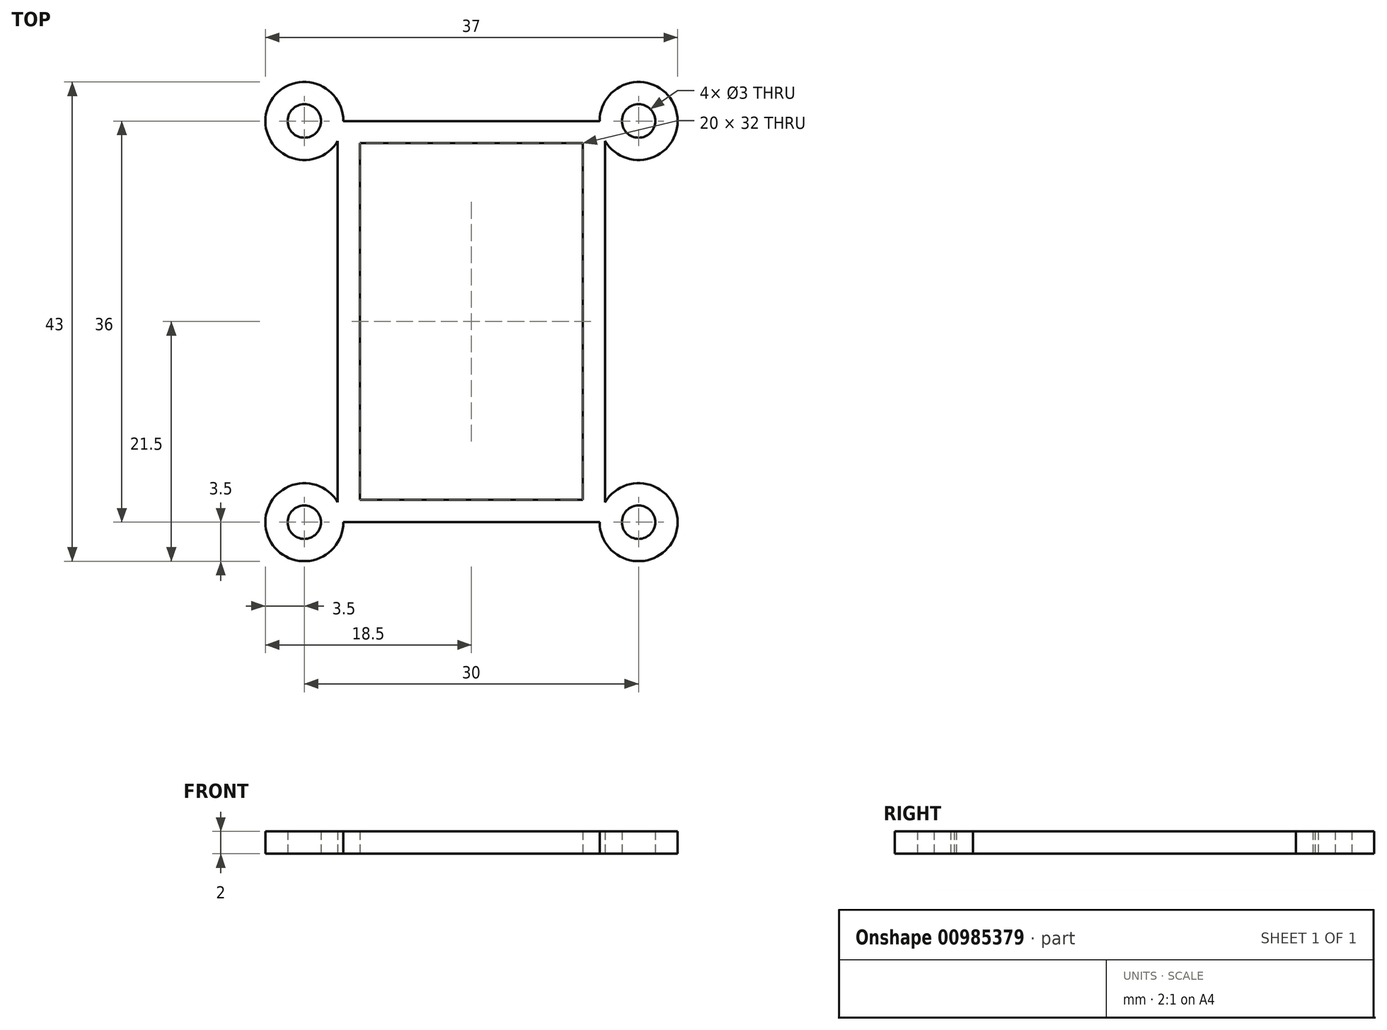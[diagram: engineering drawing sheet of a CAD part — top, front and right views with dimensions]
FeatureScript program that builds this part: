
annotation { "Feature Type Name" : "Feature", "Feature Type Description" : "" }
export const myFeature = defineFeature(function(context is Context, id is Id, definition is map)
    precondition{}
    {
        {
            var Q0;
            Q0=qCreatedBy(makeId("Top.planeOp"),FACE);
            var sketch = newSketch(context, id + "F0", { "sketchPlane" : qUnion([Q0])});
            skLineSegment(sketch, "E0.bottom", {"start": v(12, 18) * mm, "end": v(-12, 18) * mm});
            skLineSegment(sketch, "E0.top", {"start": v(12, -18) * mm, "end": v(-12, -18) * mm});
            skLineSegment(sketch, "E0.left", {"start": v(12, 18) * mm, "end": v(12, -18) * mm});
            skLineSegment(sketch, "E0.right", {"start": v(-12, 18) * mm, "end": v(-12, -18) * mm});
            skPoint(sketch, "E0.middle", {"position": v(0, 0) * mm});
            skLineSegment(sketch, "E1.bottom", {"start": v(10, 16) * mm, "end": v(-10, 16) * mm});
            skLineSegment(sketch, "E1.top", {"start": v(10, -16) * mm, "end": v(-10, -16) * mm});
            skLineSegment(sketch, "E1.left", {"start": v(10, 16) * mm, "end": v(10, -16) * mm});
            skLineSegment(sketch, "E1.right", {"start": v(-10, 16) * mm, "end": v(-10, -16) * mm});
            skLineSegment(sketch, "E2.bottom", {"start": v(15, 18) * mm, "end": v(-15, 18) * mm, "construction": true});
            skLineSegment(sketch, "E2.top", {"start": v(15, -18) * mm, "end": v(-15, -18) * mm, "construction": true});
            skLineSegment(sketch, "E2.left", {"start": v(15, 18) * mm, "end": v(15, -18) * mm, "construction": true});
            skLineSegment(sketch, "E2.right", {"start": v(-15, 18) * mm, "end": v(-15, -18) * mm, "construction": true});
            skCircle(sketch, "E3", {"center": v(-15, 18) * mm, "radius": 1.5 * mm});
            skCircle(sketch, "E4", {"center": v(15, 18) * mm, "radius": 1.5 * mm});
            skCircle(sketch, "E5", {"center": v(15, -18) * mm, "radius": 1.5 * mm});
            skCircle(sketch, "E6", {"center": v(-15, -18) * mm, "radius": 1.5 * mm});
            skCircle(sketch, "E7", {"center": v(-15, 18) * mm, "radius": 3.5 * mm});
            skCircle(sketch, "E8", {"center": v(15, 18) * mm, "radius": 3.5 * mm});
            skCircle(sketch, "E9", {"center": v(15, -18) * mm, "radius": 3.5 * mm});
            skCircle(sketch, "E10", {"center": v(-15, -18) * mm, "radius": 3.5 * mm});
            skSolve(sketch);
        }
        {
            var Q0;
            Q0 = qSketchRegion(id + "F0", true);
            extrude(context, id + "F1", {"entities" : qUnion([Q0]), "depth" : 2 * mm, "offsetDistance" : 25 * mm});
        }
    });
